# Revit family: 50085
name_source: partatom
category: Lighting Fixtures
revit_build: Autodesk Revit 2018 (Build: 20170223_1515(x64)
units: mm (PartAtom-declared; Revit-internal decimal feet)

## family parameters
Always vertical = No
Cut with Voids When Loaded = No
Light Source = No
Part Type = Normal
Room Calculation Point = No
Round Connector Dimension = Use Diameter
Shared = No
Work Plane-Based = Yes

## types (1)
- 0050085 ZEPHYR LARGE 7700LM 4K CLI GREY
    Apparent Load = 61 VA
    Assembly Code = D5020200
    Beam Angle = 67.00°
    Body Material = Diecast Aluminium Grey RAL9022
    CRI ( Ra ) = 70
    Catalog Number = 2093061 BEACON XXL WB 4K L3 WHT
    Default Elevation = 0 mm  [stored 0 ft]
    Description = Beacon XXL is an LED replacement for the traditional 70W CMI spotlights Ideal for double height spaces, retail and display applications High colour rendering index, Ra 93 or 85 typical Available in 3000K or 4000K colour temperatures Non dimmable, On-board dimming and DALI versions available Narrow (21°), Medium (50°) or Wide (67°) beam options For mounting on 3-circuit track (Lytespan 3) White or Black paint finishes as standard. Other colour available on request. Barn doors, Elongation lens, Honeycomb and Snoot accessories available IR/UV free light source without heat radiation Energy Class: A++, A+, A Long lifetime: 50,000 hours life at 70% of the original output (L70) LED technology provides an energy efficient solution with reduced maintenance costs
    Diffuser Material = UV Stabilised Polycarbonate
    Dimming Range = Non-dim / not dimmable (switched only)
    Distribution type = Medium Assymetric
    Drive Current = 750mA
    Electrical Protection = CLASS II
    Height = 96 mm  [stored 0.314961 ft]
    IK Rating = IK09
    IP Rating = IP66
    Initial Color = 4000 K
    Initial Intensity = 8800 lm
    LOR = 1
    Length = 483 mm  [stored 1.58465 ft]
    Life = 50 000h
    Light Loss Factor = 1
    Manufacturer = Feilo Sylvania
    Model = Zephyr Large 7700LM 4K CLI Grey
    Product Family = BEACON XXL - WIDE BEAM
    Ta Rating = 25
    URL = 0.9
    Voltage = 240 V
    Voltage Comments = UNV (Universal Voltage; 220-240 Volt)
    Weight = 1.50 kg
    Width = 209 mm  [stored 0.685696 ft]

note: [stored X ft] marks values corroborated as IEEE doubles in the binary element streams (Revit-internal decimal feet)

## geometry (parser evidence)
native form markers: Sweep x9
no freeform markers — native parametric forms only
